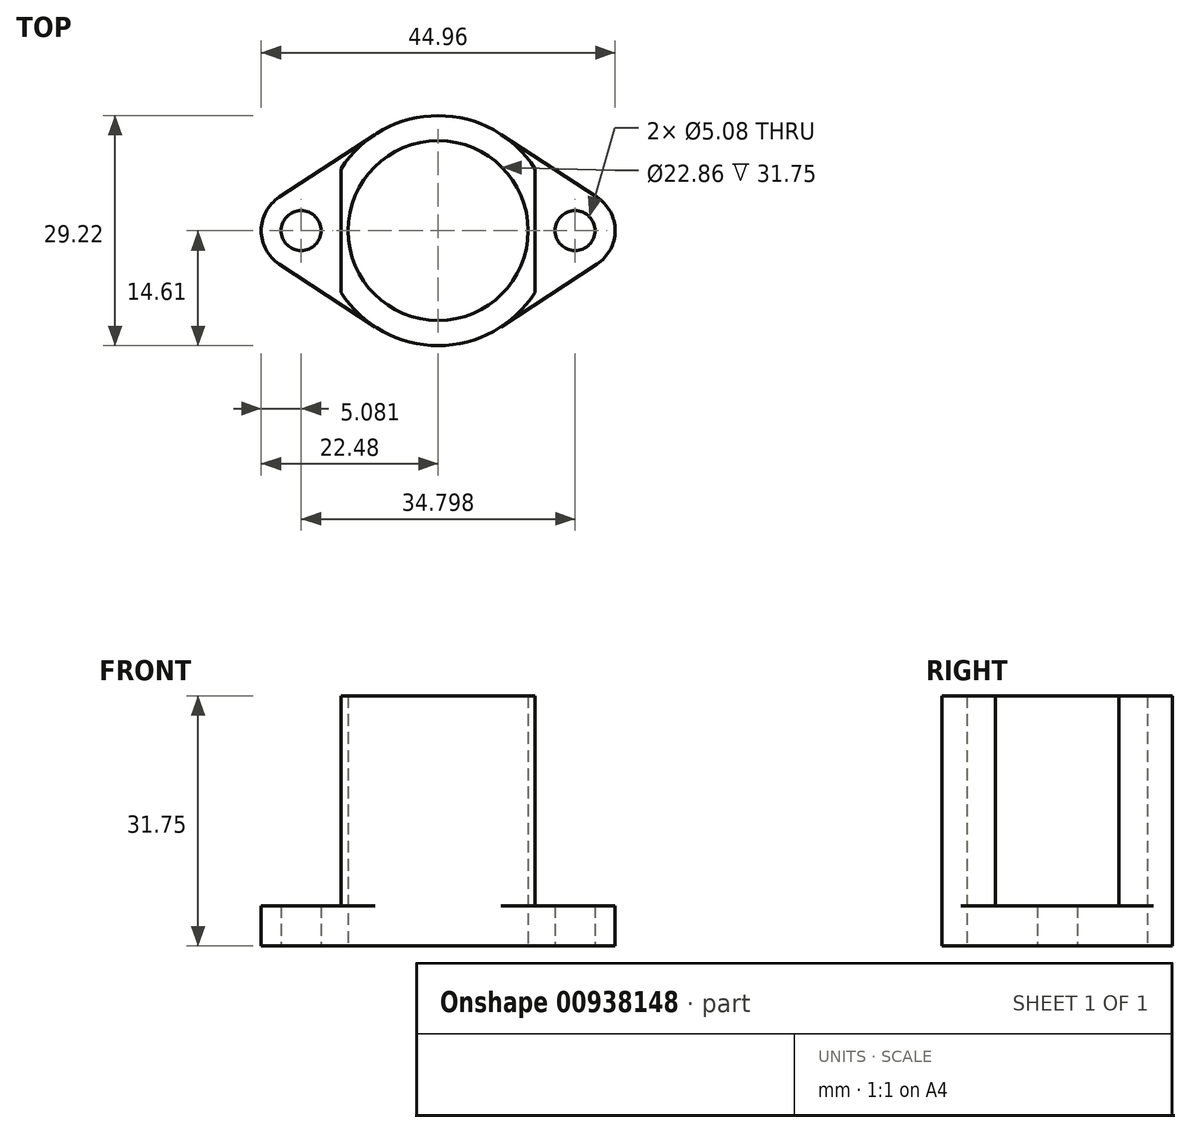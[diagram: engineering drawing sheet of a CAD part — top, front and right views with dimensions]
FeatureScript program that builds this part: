
annotation { "Feature Type Name" : "Feature", "Feature Type Description" : "" }
export const myFeature = defineFeature(function(context is Context, id is Id, definition is map)
    precondition{}
    {
        {
            var Q0;
            Q0=qCreatedBy(makeId("Top.planeOp"),FACE);
            var sketch = newSketch(context, id + "F0", { "sketchPlane" : qUnion([Q0])});
            skCircle(sketch, "E0", {"center": v(17.4, 0) * mm, "radius": 2.54 * mm});
            skCircle(sketch, "E1", {"center": v(-17.4, 0) * mm, "radius": 2.54 * mm});
            skArc(sketch, "E2", {"start": v(12.32, 7.85) * mm, "mid": v(0, 14.6) * mm, "end": v(-12.32, 7.85) * mm});
            skLineSegment(sketch, "E3.right", {"start": v(-12.32, 0) * mm, "end": v(-12.32, 7.85) * mm});
            skLineSegment(sketch, "E4.MirrorCS", {"start": v(12.32, 0) * mm, "end": v(12.32, 7.85) * mm});
            skLineSegment(sketch, "E5.MirrorCS", {"start": v(-12.32, 0) * mm, "end": v(-12.32, -7.85) * mm});
            skLineSegment(sketch, "E6.MirrorCS", {"start": v(12.32, 0) * mm, "end": v(12.32, -7.85) * mm});
            skArc(sketch, "E7.trimOffspring", {"start": v(-12.32, -7.85) * mm, "mid": v(0, -14.6) * mm, "end": v(12.32, -7.85) * mm});
            skArc(sketch, "E8", {"start": v(20.18, -4.25) * mm, "mid": v(22.48, 0) * mm, "end": v(20.18, 4.25) * mm});
            skLineSegment(sketch, "E9", {"start": v(8, 12.22) * mm, "end": v(20.18, 4.25) * mm});
            skLineSegment(sketch, "E10", {"start": v(8, -12.22) * mm, "end": v(20.18, -4.25) * mm});
            skLineSegment(sketch, "E11.MirrorCS", {"start": v(-8, 12.22) * mm, "end": v(-20.18, 4.25) * mm});
            skLineSegment(sketch, "E12.MirrorCS", {"start": v(-8, -12.22) * mm, "end": v(-20.18, -4.25) * mm});
            skArc(sketch, "E13.MirrorC", {"start": v(-20.18, -4.25) * mm, "mid": v(-22.48, 0) * mm, "end": v(-20.18, 4.25) * mm});
            skCircle(sketch, "E14", {"center": v(0, 0) * mm, "radius": 11.43 * mm});
            skSolve(sketch);
        }
        {
            var Q0;
            {var subQ9=sQuery(id+"F0.wireOp",EDGE,"E3.right");Q0=makeQuery(id+"F0.imprint","IMPRINT",FACE,{"disambiguationData":[TD([[makeQuery(id+"F0.imprint","IMPRINT",EDGE,{"derivedFrom":subQ9}),-1.0]])]});}
            var sketch = newSketch(context, id + "F1", { "sketchPlane" : qUnion([Q0])});
            skSolve(sketch);
        }
        {
            var Q0;
            Q0 = qSketchRegion(id + "F0", true);
            extrude(context, id + "F2", {"entities" : qUnion([Q0]), "depth" : 5.08 * mm, "offsetDistance" : 25.4 * mm});
        }
        {
            var Q0;
            {var subQ9=sQuery(id+"F0.wireOp",EDGE,"E3.right");Q0=makeQuery(id+"F1.imprint","IMPRINT",FACE,{"disambiguationData":[TD([[makeQuery(id+"F1.imprint","IMPRINT",EDGE,{"derivedFrom":makeQuery(id+"F0.imprint","IMPRINT",EDGE,{"derivedFrom":subQ9})}),-1.0]])]});}
            extrude(context, id + "F3", {"entities" : qUnion([Q0]), "operationType" : NewBodyOperationType.ADD, "depth" : 31.75 * mm, "offsetDistance" : 25.4 * mm});
        }
    });
